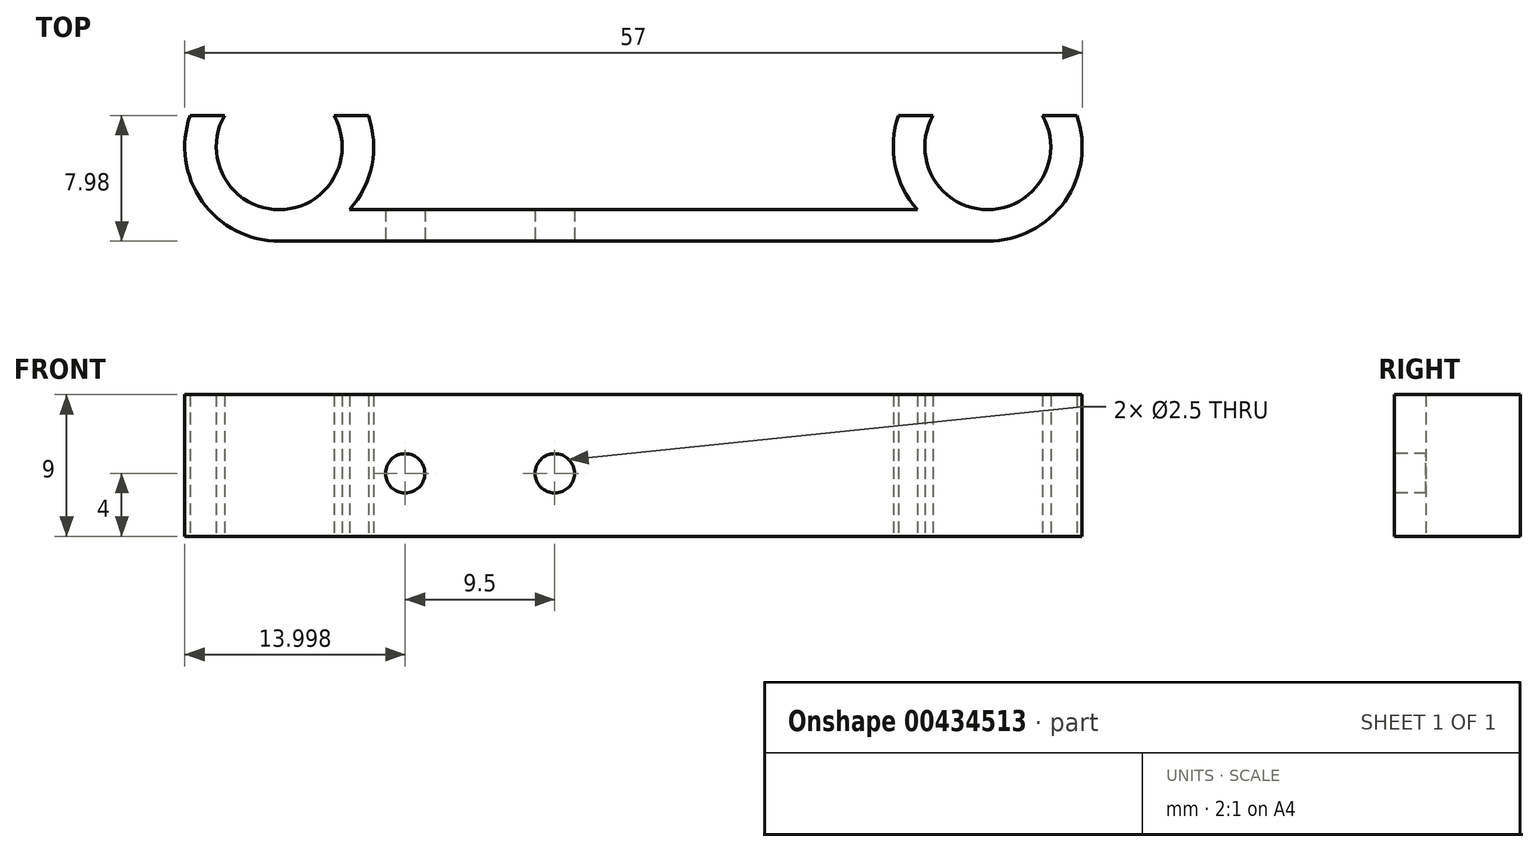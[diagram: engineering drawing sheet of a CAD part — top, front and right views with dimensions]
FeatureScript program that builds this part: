
annotation { "Feature Type Name" : "Feature", "Feature Type Description" : "" }
export const myFeature = defineFeature(function(context is Context, id is Id, definition is map)
    precondition{}
    {
        {
            var Q0;
            Q0=qCreatedBy(makeId("Top.planeOp"),FACE);
            var sketch = newSketch(context, id + "F0", { "sketchPlane" : qUnion([Q0])});
            skArc(sketch, "E0", {"start": v(-19.73, 7.98) * mm, "mid": v(-14.06, 0) * mm, "end": v(-8.4, 7.98) * mm});
            skLineSegment(sketch, "E1.right", {"start": v(278.54, 89.36) * mm, "end": v(278.54, 0) * mm});
            skArc(sketch, "E2", {"start": v(-17.54, 7.98) * mm, "mid": v(-14.06, 2) * mm, "end": v(-10.59, 7.98) * mm});
            skLineSegment(sketch, "E3.top", {"start": v(-19.73, 7.98) * mm, "end": v(-17.54, 7.98) * mm});
            skLineSegment(sketch, "E4.trimOffspring", {"start": v(-10.59, 7.98) * mm, "end": v(-8.4, 7.98) * mm});
            skArc(sketch, "E5", {"start": v(25.27, 7.98) * mm, "mid": v(30.94, 0) * mm, "end": v(36.6, 7.98) * mm});
            skArc(sketch, "E6", {"start": v(27.46, 7.98) * mm, "mid": v(30.94, 2) * mm, "end": v(34.41, 7.98) * mm});
            skLineSegment(sketch, "E7.top", {"start": v(25.27, 7.98) * mm, "end": v(27.46, 7.98) * mm});
            skLineSegment(sketch, "E8.trimOffspring", {"start": v(34.41, 7.98) * mm, "end": v(36.6, 7.98) * mm});
            skLineSegment(sketch, "E9.bottom", {"start": v(-14.06, 0) * mm, "end": v(30.94, 0) * mm});
            skLineSegment(sketch, "E10", {"start": v(-14.06, 0) * mm, "end": v(-14.06, 2) * mm});
            skLineSegment(sketch, "E11", {"start": v(-14.06, 2) * mm, "end": v(30.94, 2) * mm});
            skLineSegment(sketch, "E12", {"start": v(30.94, 2) * mm, "end": v(30.94, 0) * mm});
            skLineSegment(sketch, "E13", {"start": v(-18.06, 6) * mm, "end": v(41.26, 6) * mm, "construction": true});
            skPoint(sketch, "E14", {"position": v(34.94, 6) * mm});
            skSolve(sketch);
        }
        {
            var Q0;
            Q0=qSketchRegion(id+"F0",true);
            extrude(context, id + "F1", {"entities" : qUnion([Q0]), "depth" : 9 * mm});
        }
        {
            var Q0;
            Q0=qCreatedBy(makeId("Front.planeOp"),FACE);
            var sketch = newSketch(context, id + "F2", { "sketchPlane" : qUnion([Q0])});
            skCircle(sketch, "E15", {"center": v(-6.06, 4) * mm, "radius": 1.25 * mm});
            skCircle(sketch, "E16", {"center": v(3.44, 4) * mm, "radius": 1.25 * mm});
            skSolve(sketch);
        }
        {
            var Q0;
            Q0=qSketchRegion(id+"F2",true);
            extrude(context, id + "F3", {"entities" : qUnion([Q0]), "operationType" : NewBodyOperationType.REMOVE, "oppositeDirection" : true, "depth" : 2 * mm});
        }
    });
